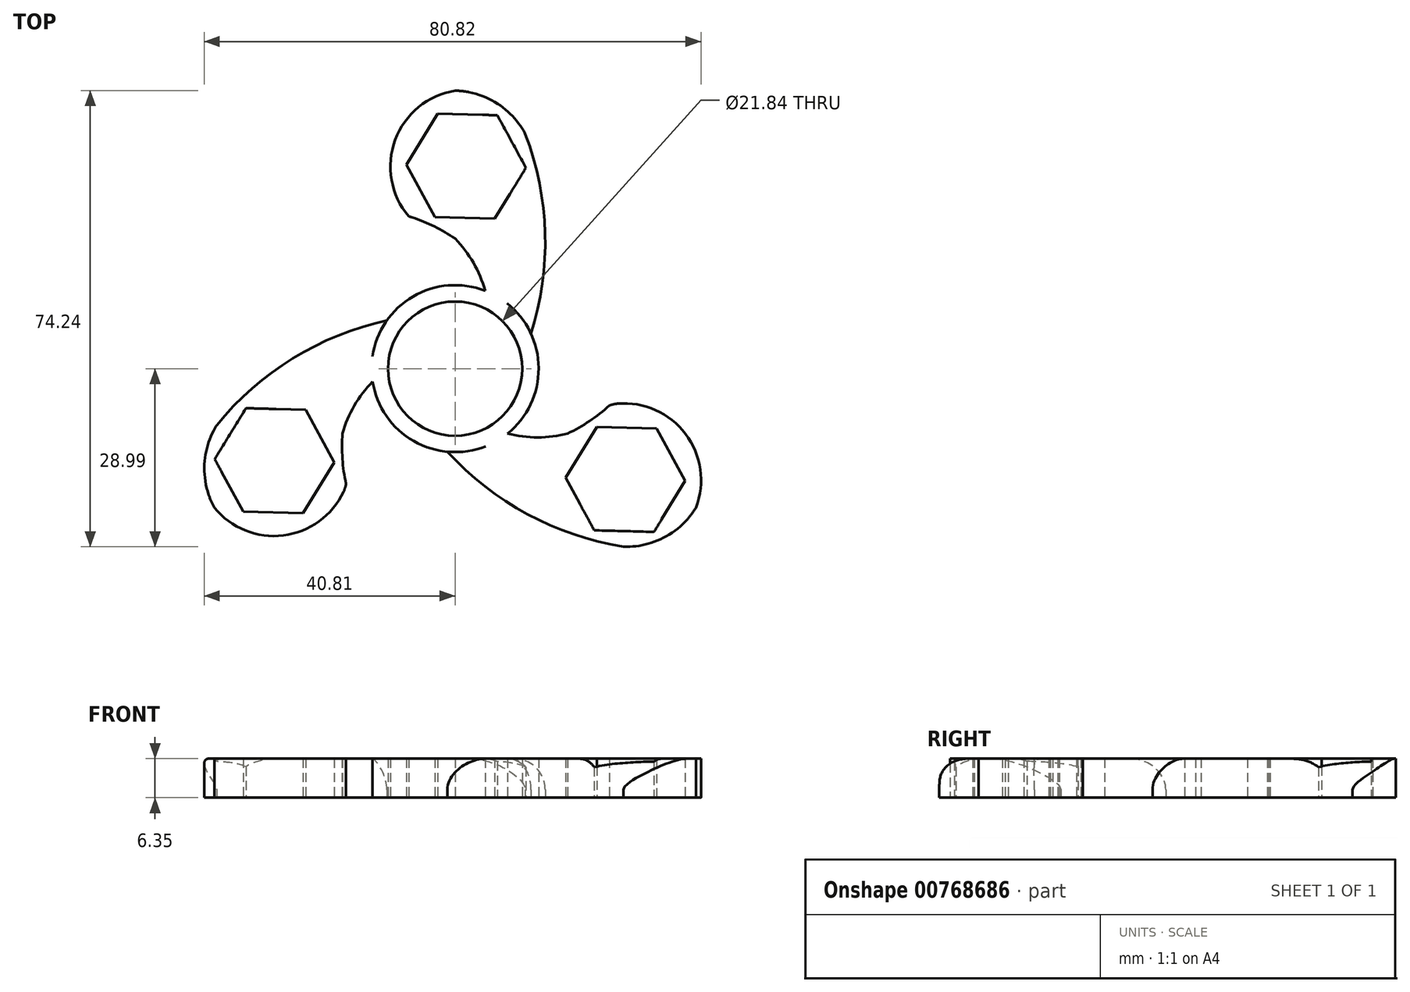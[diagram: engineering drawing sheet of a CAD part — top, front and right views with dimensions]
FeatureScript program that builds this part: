
annotation { "Feature Type Name" : "Feature", "Feature Type Description" : "" }
export const myFeature = defineFeature(function(context is Context, id is Id, definition is map)
    precondition{}
    {
        {
            var Q0;
            Q0=qCreatedBy(makeId("Top.planeOp"),FACE);
            var sketch = newSketch(context, id + "F0", { "sketchPlane" : qUnion([Q0])});
            skCircle(sketch, "E0", {"center": v(0, 0) * mm, "radius": 10.92 * mm});
            skLineSegment(sketch, "E1", {"start": v(0, 0) * mm, "end": v(0, 43.99) * mm, "construction": true});
            skCircle(sketch, "E2.cCircle", {"center": v(1.79, 32.95) * mm, "radius": 9.73 * mm, "construction": true});
            skLineSegment(sketch, "E2.0", {"start": v(6.43, 24.4) * mm, "end": v(-3.3, 24.65) * mm});
            skLineSegment(sketch, "E2.1", {"start": v(-3.3, 24.65) * mm, "end": v(-7.94, 33.2) * mm});
            skLineSegment(sketch, "E2.2", {"start": v(-7.94, 33.2) * mm, "end": v(-2.85, 41.5) * mm});
            skLineSegment(sketch, "E2.3", {"start": v(-2.85, 41.5) * mm, "end": v(6.88, 41.24) * mm});
            skLineSegment(sketch, "E2.4", {"start": v(6.88, 41.24) * mm, "end": v(11.52, 32.69) * mm});
            skLineSegment(sketch, "E2.5", {"start": v(11.52, 32.69) * mm, "end": v(6.43, 24.4) * mm});
            skLineSegment(sketch, "E3.1.0", {"start": v(0, 0) * mm, "end": v(-38.1, -22) * mm, "construction": true});
            skLineSegment(sketch, "E3.2.0", {"start": v(0, 0) * mm, "end": v(37.22, -21.49) * mm, "construction": true});
            skPoint(sketch, "E4.endSnap0", {"position": v(-7.42, 30.26) * mm});
            skCircle(sketch, "E5", {"center": v(1.03, 32.95) * mm, "radius": 3.99 * mm});
            skCircle(sketch, "E6", {"center": v(0, 0) * mm, "radius": 4.64 * mm});
            skCircle(sketch, "E7", {"center": v(0, 0) * mm, "radius": 9.88 * mm});
            skArc(sketch, "E8.1.2", {"start": v(-6.87, 8.59) * mm, "mid": v(-21.48, 4.32) * mm, "end": v(-34.1, -4.2) * mm});
            skCircle(sketch, "E9", {"center": v(0, 0) * mm, "radius": 13.59 * mm});
            skLineSegment(sketch, "E10.trimOffspring", {"start": v(37.34, -21.56) * mm, "end": v(38.1, -22) * mm, "construction": true});
            skPoint(sketch, "E11.orphan", {"position": v(-6.57, 25.15) * mm});
            skPoint(sketch, "E12.orphan", {"position": v(-18.5, -18.27) * mm});
            skArc(sketch, "E13.2.2", {"start": v(-4, -10.24) * mm, "mid": v(10.08, -22.74) * mm, "end": v(27.82, -29.06) * mm});
            skCircle(sketch, "E14.2.7", {"center": v(28.02, -17.36) * mm, "radius": 3.99 * mm});
            skPoint(sketch, "E15.orphan", {"position": v(-38.7, -15.33) * mm});
            skCircle(sketch, "E16.1.0", {"center": v(-29, -15.65) * mm, "radius": 3.99 * mm});
            skLineSegment(sketch, "E16.1.1", {"start": v(-19.66, -15.25) * mm, "end": v(-24.75, -23.54) * mm});
            skCircle(sketch, "E16.1.2", {"center": v(-29.39, -15) * mm, "radius": 9.73 * mm, "construction": true});
            skLineSegment(sketch, "E16.1.3", {"start": v(-24.3, -6.7) * mm, "end": v(-19.66, -15.25) * mm});
            skLineSegment(sketch, "E16.1.4", {"start": v(-34.03, -6.44) * mm, "end": v(-24.3, -6.7) * mm});
            skLineSegment(sketch, "E16.1.5", {"start": v(-39.12, -14.73) * mm, "end": v(-34.03, -6.44) * mm});
            skLineSegment(sketch, "E16.1.6", {"start": v(-34.48, -23.28) * mm, "end": v(-39.12, -14.73) * mm});
            skLineSegment(sketch, "E16.1.7", {"start": v(-24.75, -23.54) * mm, "end": v(-34.48, -23.28) * mm});
            skCircle(sketch, "E16.2.0", {"center": v(28.1, -17.36) * mm, "radius": 3.99 * mm});
            skLineSegment(sketch, "E16.2.1", {"start": v(23.07, -9.47) * mm, "end": v(32.8, -9.73) * mm});
            skCircle(sketch, "E16.2.2", {"center": v(27.71, -18.02) * mm, "radius": 9.73 * mm, "construction": true});
            skLineSegment(sketch, "E16.2.3", {"start": v(17.99, -17.77) * mm, "end": v(23.07, -9.47) * mm});
            skLineSegment(sketch, "E16.2.4", {"start": v(22.63, -26.32) * mm, "end": v(17.99, -17.77) * mm});
            skLineSegment(sketch, "E16.2.5", {"start": v(32.35, -26.58) * mm, "end": v(22.63, -26.32) * mm});
            skLineSegment(sketch, "E16.2.6", {"start": v(37.44, -18.28) * mm, "end": v(32.35, -26.58) * mm});
            skLineSegment(sketch, "E16.2.7", {"start": v(32.8, -9.73) * mm, "end": v(37.44, -18.28) * mm});
            skPoint(sketch, "E16.center", {"position": v(0.04, -0.02) * mm});
            skPoint(sketch, "E17.orphan", {"position": v(21.89, -9.12) * mm});
            skPoint(sketch, "E18.orphan", {"position": v(0, 21.15) * mm});
            skArc(sketch, "E19.1.2", {"start": v(10.87, 1.66) * mm, "mid": v(14.66, 20.1) * mm, "end": v(11.25, 38.62) * mm});
            skArc(sketch, "E19.2.2", {"start": v(-6.87, 8.59) * mm, "mid": v(-24.74, 2.64) * mm, "end": v(-39.07, -9.56) * mm});
            skPoint(sketch, "E20.orphan", {"position": v(-12.06, -1.2) * mm});
            skArc(sketch, "E21", {"start": v(-10.92, 0) * mm, "mid": v(-15.53, -4.65) * mm, "end": v(-18.31, -10.57) * mm});
            skArc(sketch, "E22", {"start": v(-18.22, -10.23) * mm, "mid": v(-18.27, -10.4) * mm, "end": v(-18.31, -10.57) * mm});
            skArc(sketch, "E23.1.0", {"start": v(5.46, -9.46) * mm, "mid": v(11.8, -11.13) * mm, "end": v(18.31, -10.57) * mm});
            skArc(sketch, "E23.1.1", {"start": v(17.97, -10.66) * mm, "mid": v(18.14, -10.62) * mm, "end": v(18.31, -10.57) * mm});
            skArc(sketch, "E23.2.0", {"start": v(5.46, 9.46) * mm, "mid": v(3.74, 15.77) * mm, "end": v(0, 21.15) * mm});
            skArc(sketch, "E23.2.1", {"start": v(0.25, 20.89) * mm, "mid": v(0.13, 21.02) * mm, "end": v(0, 21.15) * mm});
            skPoint(sketch, "E24", {"position": v(-34.1, -4.2) * mm});
            skLineSegment(sketch, "E25", {"start": v(0, 43.99) * mm, "end": v(0, 50.14) * mm, "construction": true});
            skArc(sketch, "E26", {"start": v(11.41, 38.2) * mm, "mid": v(6.66, 43.27) * mm, "end": v(0, 45.25) * mm});
            skArc(sketch, "E27", {"start": v(0, 45.25) * mm, "mid": v(-9.76, 37.23) * mm, "end": v(-7.55, 24.8) * mm});
            skArc(sketch, "E28", {"start": v(-7.55, 24.8) * mm, "mid": v(-7.46, 24.74) * mm, "end": v(-7.35, 24.73) * mm});
            skPoint(sketch, "E29.trimOffspring.end.orphan", {"position": v(-7.42, 24.64) * mm});
            skArc(sketch, "E30.1.0", {"start": v(-17.7, -18.94) * mm, "mid": v(-17.7, -18.83) * mm, "end": v(-17.74, -18.73) * mm});
            skArc(sketch, "E30.1.1", {"start": v(-39.18, -22.62) * mm, "mid": v(-27.36, -27.06) * mm, "end": v(-17.7, -18.94) * mm});
            skArc(sketch, "E30.1.2", {"start": v(-38.8, -9.22) * mm, "mid": v(-40.8, -15.87) * mm, "end": v(-39.18, -22.62) * mm});
            skArc(sketch, "E30.2.0", {"start": v(25.25, -5.86) * mm, "mid": v(25.16, -5.92) * mm, "end": v(25.1, -6) * mm});
            skArc(sketch, "E30.2.1", {"start": v(39.18, -22.62) * mm, "mid": v(37.12, -10.17) * mm, "end": v(25.25, -5.86) * mm});
            skArc(sketch, "E30.2.2", {"start": v(27.38, -28.99) * mm, "mid": v(34.14, -27.4) * mm, "end": v(39.18, -22.62) * mm});
            skPoint(sketch, "E31.orphan", {"position": v(23.9, -7.36) * mm});
            skArc(sketch, "E32", {"start": v(18.31, -10.57) * mm, "mid": v(21.87, -8.54) * mm, "end": v(25.1, -6) * mm});
            skPoint(sketch, "E33.orphan", {"position": v(-5.58, 24.38) * mm});
            skArc(sketch, "E34.1.1", {"start": v(0, 21.15) * mm, "mid": v(-3.54, 23.21) * mm, "end": v(-7.35, 24.73) * mm});
            skPoint(sketch, "E34.2.0", {"position": v(-18.33, -17.02) * mm});
            skArc(sketch, "E34.2.1", {"start": v(-18.31, -10.57) * mm, "mid": v(-18.33, -14.67) * mm, "end": v(-17.74, -18.73) * mm});
            skLineSegment(sketch, "E35", {"start": v(0.04, -0.02) * mm, "end": v(24.36, 21.28) * mm, "construction": true});
            skSolve(sketch);
        }
        {
            var Q0;
            Q0 = qSketchRegion(id + "F0", true);
            extrude(context, id + "F1", {"entities" : qUnion([Q0]), "depth" : 6.35 * mm, "offsetDistance" : 25.4 * mm});
        }
        {
            var Q0;
            Q0=makeQuery(id+"F1.opExtrude","CAP_EDGE",EDGE,{"disambiguationData":[OSD([sQuery(id+"F0.wireOp",EDGE,"E19.2.2")])],"isStart":false});
            var Q1;
            Q1=makeQuery(id+"F1.opExtrude","CAP_EDGE",EDGE,{"disambiguationData":[OSD([sQuery(id+"F0.wireOp",EDGE,"E13.2.2")])],"isStart":false});
            var Q2;
            Q2=makeQuery(id+"F1.opExtrude","CAP_EDGE",EDGE,{"disambiguationData":[OSD([sQuery(id+"F0.wireOp",EDGE,"E19.1.2")])],"isStart":false});
            var Q3;
            Q3=makeQuery(id+"F1.opExtrude","SWEPT_EDGE",EDGE,{"disambiguationData":[OSD([sQuery(id+"F0.wireOp",EDGE,"E28"),sQuery(id+"F0.wireOp",EDGE,"E34.1.1")])]});
            var Q4;
            Q4=makeQuery(id+"F1.opExtrude","SWEPT_EDGE",EDGE,{"disambiguationData":[OSD([sQuery(id+"F0.wireOp",EDGE,"E30.1.0"),sQuery(id+"F0.wireOp",EDGE,"E30.1.1")])]});
            var Q5;
            Q5=makeQuery(id+"F1.opExtrude","SWEPT_EDGE",EDGE,{"disambiguationData":[OSD([sQuery(id+"F0.wireOp",EDGE,"E30.2.0"),sQuery(id+"F0.wireOp",EDGE,"E30.2.1")])]});
            fillet(context, id + "F2", {"entities" : qUnion([Q0, Q1, Q2, Q3, Q4, Q5]), "radius" : 5.08 * mm, "tangentPropagation" : true, "allowEdgeOverflow" : false});
        }
    });
